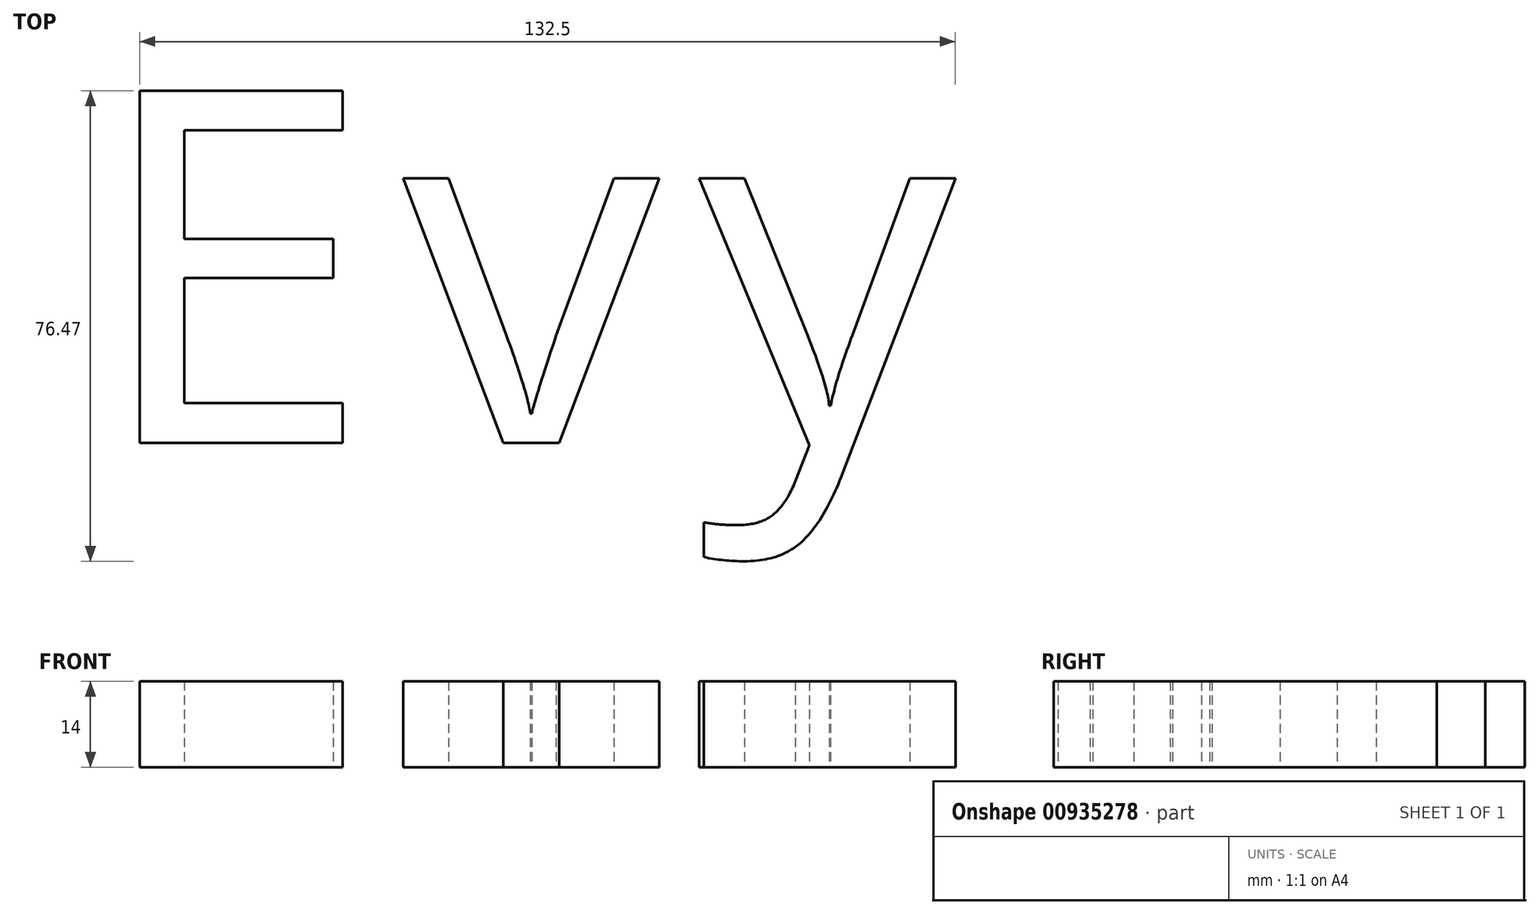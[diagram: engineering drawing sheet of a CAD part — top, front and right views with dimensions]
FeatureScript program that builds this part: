
annotation { "Feature Type Name" : "Feature", "Feature Type Description" : "" }
export const myFeature = defineFeature(function(context is Context, id is Id, definition is map)
    precondition{}
    {
        {
            var Q0;
            Q0=qCreatedBy(makeId("Top.planeOp"),FACE);
            var sketch = newSketch(context, id + "F0", { "sketchPlane" : qUnion([Q0])});
            skText(sketch, "E0", { "text": "Evy", "fontName": "DroidSansMono.ttf"});
            const initialGuessF0  = {"E0": [-0.08128, -0.02671, 1, 0, 0.0577]};
            skSetInitialGuess(sketch, initialGuessF0);
            skSolve(sketch);
        }
        {
            var Q0;
            Q0=makeQuery(id+"F0.imprint","IMPRINT",FACE,{"disambiguationData":[TD([[makeQuery(id+"F0.imprint","IMPRINT",EDGE,{"derivedFrom":sQuery(id+"F0.wireOp",EDGE,"E0.sketch_text.stroke-0")}),-1.0]])]});
            var Q1;
            Q1 = qSketchRegion(id + "F0", true);
            extrude(context, id + "F1", {"entities" : qUnion([Q0, Q1]), "depth" : 14 * mm, "offsetDistance" : 25 * mm});
        }
    });
